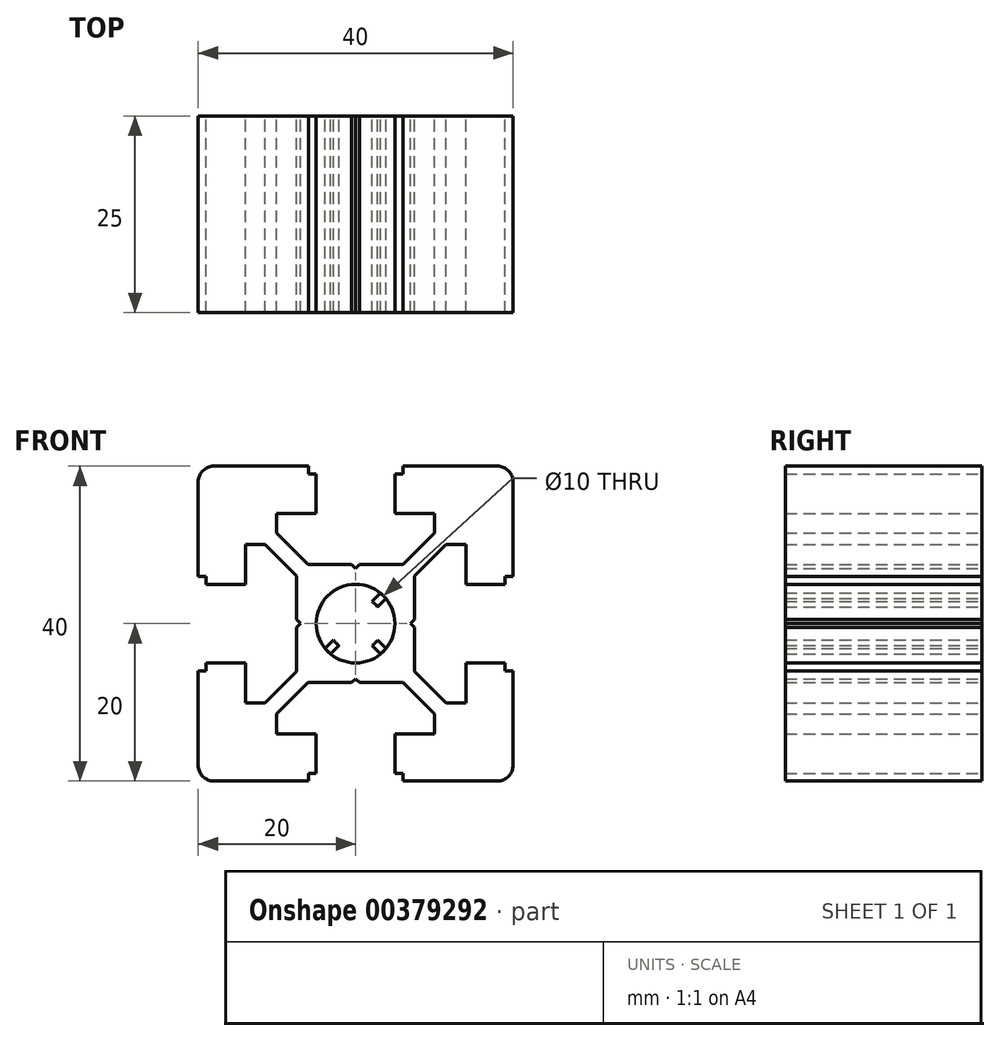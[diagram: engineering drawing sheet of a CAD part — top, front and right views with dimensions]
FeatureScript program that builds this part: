
annotation { "Feature Type Name" : "Feature", "Feature Type Description" : "" }
export const myFeature = defineFeature(function(context is Context, id is Id, definition is map)
    precondition{}
    {
        {
            var Q0;
            Q0=qCreatedBy(makeId("Front.planeOp"),FACE);
            var sketch = newSketch(context, id + "F0", { "sketchPlane" : qUnion([Q0])});
            skLineSegment(sketch, "E0.bottom", {"start": v(2, 0) * mm, "end": v(38, 0) * mm});
            skLineSegment(sketch, "E0.top", {"start": v(2, 40) * mm, "end": v(38, 40) * mm});
            skLineSegment(sketch, "E0.left", {"start": v(0, 2) * mm, "end": v(0, 38) * mm});
            skLineSegment(sketch, "E0.right", {"start": v(40, 2) * mm, "end": v(40, 38) * mm});
            skPoint(sketch, "E1.visualSharp", {"position": v(40, 40) * mm});
            skArc(sketch, "E1.filletArc", {"start": v(40, 38) * mm, "mid": v(39.41, 39.41) * mm, "end": v(38, 40) * mm});
            skPoint(sketch, "E2.visualSharp", {"position": v(0, 40) * mm});
            skArc(sketch, "E2.filletArc", {"start": v(2, 40) * mm, "mid": v(0.59, 39.41) * mm, "end": v(0, 38) * mm});
            skPoint(sketch, "E3.visualSharp", {"position": v(0, 0) * mm});
            skArc(sketch, "E3.filletArc", {"start": v(0, 2) * mm, "mid": v(0.59, 0.59) * mm, "end": v(2, 0) * mm});
            skPoint(sketch, "E4.visualSharp", {"position": v(40, 0) * mm});
            skArc(sketch, "E4.filletArc", {"start": v(38, 0) * mm, "mid": v(39.41, 0.59) * mm, "end": v(40, 2) * mm});
            skLineSegment(sketch, "E5", {"start": v(0, 0) * mm, "end": v(40, 40) * mm, "construction": true});
            skLineSegment(sketch, "E6", {"start": v(0, 40) * mm, "end": v(40, 0) * mm, "construction": true});
            skCircle(sketch, "E7", {"center": v(20, 20) * mm, "radius": 5 * mm});
            skCircle(sketch, "E8", {"center": v(20, 20) * mm, "radius": 3.5 * mm});
            skLineSegment(sketch, "E9.bottom", {"start": v(16.13, 16.84) * mm, "end": v(16.84, 16.13) * mm});
            skLineSegment(sketch, "E9.top", {"start": v(23.16, 23.87) * mm, "end": v(23.87, 23.16) * mm});
            skLineSegment(sketch, "E9.left", {"start": v(16.13, 16.84) * mm, "end": v(23.16, 23.87) * mm});
            skLineSegment(sketch, "E9.right", {"start": v(16.84, 16.13) * mm, "end": v(23.87, 23.16) * mm});
            skLineSegment(sketch, "E10.bottom", {"start": v(16.13, 23.16) * mm, "end": v(16.84, 23.87) * mm});
            skLineSegment(sketch, "E10.top", {"start": v(23.16, 16.13) * mm, "end": v(23.87, 16.84) * mm});
            skLineSegment(sketch, "E10.left", {"start": v(16.13, 23.16) * mm, "end": v(23.16, 16.13) * mm});
            skLineSegment(sketch, "E10.right", {"start": v(16.84, 23.87) * mm, "end": v(23.87, 16.84) * mm});
            skLineSegment(sketch, "E11", {"start": v(14, 40) * mm, "end": v(14, 39) * mm});
            skLineSegment(sketch, "E12", {"start": v(14, 39) * mm, "end": v(15, 39) * mm});
            skLineSegment(sketch, "E13", {"start": v(15, 39) * mm, "end": v(15, 34) * mm});
            skLineSegment(sketch, "E14", {"start": v(15, 34) * mm, "end": v(9.95, 34) * mm});
            skLineSegment(sketch, "E15", {"start": v(9.95, 34) * mm, "end": v(9.95, 31.5) * mm});
            skLineSegment(sketch, "E16", {"start": v(13.95, 27.5) * mm, "end": v(9.95, 31.5) * mm});
            skLineSegment(sketch, "E17", {"start": v(13.95, 27.5) * mm, "end": v(26.05, 27.5) * mm});
            skLineSegment(sketch, "E18", {"start": v(26.05, 27.5) * mm, "end": v(30.05, 31.5) * mm});
            skLineSegment(sketch, "E19", {"start": v(30.05, 31.5) * mm, "end": v(30.05, 34) * mm});
            skLineSegment(sketch, "E20", {"start": v(30.05, 34) * mm, "end": v(25, 34) * mm});
            skLineSegment(sketch, "E21", {"start": v(25, 34) * mm, "end": v(25, 39) * mm});
            skLineSegment(sketch, "E22", {"start": v(25, 39) * mm, "end": v(26, 39) * mm});
            skLineSegment(sketch, "E23", {"start": v(26, 39) * mm, "end": v(26, 40) * mm});
            skLineSegment(sketch, "E24", {"start": v(20, 40) * mm, "end": v(20, -1.4) * mm, "construction": true});
            skLineSegment(sketch, "E25.1.0", {"start": v(6, 9.95) * mm, "end": v(8.5, 9.95) * mm});
            skLineSegment(sketch, "E25.1.1", {"start": v(6, 15) * mm, "end": v(6, 9.95) * mm});
            skLineSegment(sketch, "E25.1.2", {"start": v(1, 15) * mm, "end": v(6, 15) * mm});
            skLineSegment(sketch, "E25.1.3", {"start": v(1, 14) * mm, "end": v(1, 15) * mm});
            skLineSegment(sketch, "E25.1.4", {"start": v(0, 14) * mm, "end": v(1, 14) * mm});
            skLineSegment(sketch, "E25.1.5", {"start": v(12.5, 13.95) * mm, "end": v(8.5, 9.95) * mm});
            skLineSegment(sketch, "E25.1.6", {"start": v(12.5, 13.95) * mm, "end": v(12.5, 26.05) * mm});
            skLineSegment(sketch, "E25.1.7", {"start": v(12.5, 26.05) * mm, "end": v(8.5, 30.05) * mm});
            skLineSegment(sketch, "E25.1.8", {"start": v(8.5, 30.05) * mm, "end": v(6, 30.05) * mm});
            skLineSegment(sketch, "E25.1.9", {"start": v(6, 30.05) * mm, "end": v(6, 25) * mm});
            skLineSegment(sketch, "E25.1.10", {"start": v(6, 25) * mm, "end": v(1, 25) * mm});
            skLineSegment(sketch, "E25.1.11", {"start": v(1, 25) * mm, "end": v(1, 26) * mm});
            skLineSegment(sketch, "E25.1.12", {"start": v(1, 26) * mm, "end": v(0, 26) * mm});
            skLineSegment(sketch, "E25.2.0", {"start": v(30.05, 6) * mm, "end": v(30.05, 8.5) * mm});
            skLineSegment(sketch, "E25.2.1", {"start": v(25, 6) * mm, "end": v(30.05, 6) * mm});
            skLineSegment(sketch, "E25.2.2", {"start": v(25, 1) * mm, "end": v(25, 6) * mm});
            skLineSegment(sketch, "E25.2.3", {"start": v(26, 1) * mm, "end": v(25, 1) * mm});
            skLineSegment(sketch, "E25.2.4", {"start": v(26, 0) * mm, "end": v(26, 1) * mm});
            skLineSegment(sketch, "E25.2.5", {"start": v(26.05, 12.5) * mm, "end": v(30.05, 8.5) * mm});
            skLineSegment(sketch, "E25.2.6", {"start": v(26.05, 12.5) * mm, "end": v(13.95, 12.5) * mm});
            skLineSegment(sketch, "E25.2.7", {"start": v(13.95, 12.5) * mm, "end": v(9.95, 8.5) * mm});
            skLineSegment(sketch, "E25.2.8", {"start": v(9.95, 8.5) * mm, "end": v(9.95, 6) * mm});
            skLineSegment(sketch, "E25.2.9", {"start": v(9.95, 6) * mm, "end": v(15, 6) * mm});
            skLineSegment(sketch, "E25.2.10", {"start": v(15, 6) * mm, "end": v(15, 1) * mm});
            skLineSegment(sketch, "E25.2.11", {"start": v(15, 1) * mm, "end": v(14, 1) * mm});
            skLineSegment(sketch, "E25.2.12", {"start": v(14, 1) * mm, "end": v(14, 0) * mm});
            skLineSegment(sketch, "E25.3.0", {"start": v(34, 30.05) * mm, "end": v(31.5, 30.05) * mm});
            skLineSegment(sketch, "E25.3.1", {"start": v(34, 25) * mm, "end": v(34, 30.05) * mm});
            skLineSegment(sketch, "E25.3.2", {"start": v(39, 25) * mm, "end": v(34, 25) * mm});
            skLineSegment(sketch, "E25.3.3", {"start": v(39, 26) * mm, "end": v(39, 25) * mm});
            skLineSegment(sketch, "E25.3.4", {"start": v(40, 26) * mm, "end": v(39, 26) * mm});
            skLineSegment(sketch, "E25.3.5", {"start": v(27.5, 26.05) * mm, "end": v(31.5, 30.05) * mm});
            skLineSegment(sketch, "E25.3.6", {"start": v(27.5, 26.05) * mm, "end": v(27.5, 13.95) * mm});
            skLineSegment(sketch, "E25.3.7", {"start": v(27.5, 13.95) * mm, "end": v(31.5, 9.95) * mm});
            skLineSegment(sketch, "E25.3.8", {"start": v(31.5, 9.95) * mm, "end": v(34, 9.95) * mm});
            skLineSegment(sketch, "E25.3.9", {"start": v(34, 9.95) * mm, "end": v(34, 15) * mm});
            skLineSegment(sketch, "E25.3.10", {"start": v(34, 15) * mm, "end": v(39, 15) * mm});
            skLineSegment(sketch, "E25.3.11", {"start": v(39, 15) * mm, "end": v(39, 14) * mm});
            skLineSegment(sketch, "E25.3.12", {"start": v(39, 14) * mm, "end": v(40, 14) * mm});
            skLineSegment(sketch, "E26", {"start": v(19.5, 27.5) * mm, "end": v(20, 27) * mm});
            skLineSegment(sketch, "E27", {"start": v(20, 27) * mm, "end": v(20.5, 27.5) * mm});
            skLineSegment(sketch, "E28.1.0", {"start": v(13, 20) * mm, "end": v(12.5, 20.5) * mm});
            skLineSegment(sketch, "E28.1.1", {"start": v(12.5, 19.5) * mm, "end": v(13, 20) * mm});
            skLineSegment(sketch, "E28.2.0", {"start": v(20, 13) * mm, "end": v(19.5, 12.5) * mm});
            skLineSegment(sketch, "E28.2.1", {"start": v(20.5, 12.5) * mm, "end": v(20, 13) * mm});
            skLineSegment(sketch, "E28.3.0", {"start": v(27, 20) * mm, "end": v(27.5, 19.5) * mm});
            skLineSegment(sketch, "E28.3.1", {"start": v(27.5, 20.5) * mm, "end": v(27, 20) * mm});
            skSolve(sketch);
        }
        {
            var Q0;
            {var subQ2=sQuery(id+"F0.wireOp",EDGE,"E1.filletArc");Q0=makeQuery(id+"F0.imprint","IMPRINT",FACE,{"disambiguationData":[TD([[makeQuery(id+"F0.imprint","IMPRINT",EDGE,{"derivedFrom":subQ2}),1.0]])]});}
            var Q1;
            {var subQ3=sQuery(id+"F0.wireOp",EDGE,"E10.left");var subQ5=sQuery(id+"F0.wireOp",EDGE,"E8");var subQ7=makeQuery(id+"F0.imprint","INTERSECT",VERTEX,{"disambiguationData":[OD(0.0)],"derivedFrom":[subQ5,subQ3]});Q1=makeQuery(id+"F0.imprint","IMPRINT",FACE,{"disambiguationData":[TD([[makeQuery(id+"F0.imprint","IMPRINT",EDGE,{"disambiguationData":[TD([[subQ7,-1.0]])],"derivedFrom":subQ5}),-1.0]])]});}
            var Q2;
            {var subQ0=sQuery(id+"F0.wireOp",EDGE,"E9.right");var subQ5=sQuery(id+"F0.wireOp",EDGE,"E8");var subQ6=makeQuery(id+"F0.imprint","INTERSECT",VERTEX,{"disambiguationData":[OD(1.0)],"derivedFrom":[subQ5,subQ0]});Q2=makeQuery(id+"F0.imprint","IMPRINT",FACE,{"disambiguationData":[TD([[makeQuery(id+"F0.imprint","IMPRINT",EDGE,{"disambiguationData":[TD([[subQ6,-1.0]])],"derivedFrom":subQ5}),-1.0]])]});}
            var Q3;
            {var subQ0=sQuery(id+"F0.wireOp",EDGE,"E9.right");var subQ5=sQuery(id+"F0.wireOp",EDGE,"E8");var subQ6=makeQuery(id+"F0.imprint","INTERSECT",VERTEX,{"disambiguationData":[OD(0.0)],"derivedFrom":[subQ5,subQ0]});Q3=makeQuery(id+"F0.imprint","IMPRINT",FACE,{"disambiguationData":[TD([[makeQuery(id+"F0.imprint","IMPRINT",EDGE,{"disambiguationData":[TD([[subQ6,1.0]])],"derivedFrom":subQ5}),-1.0]])]});}
            var Q4;
            {var subQ0=sQuery(id+"F0.wireOp",EDGE,"E9.left");var subQ5=sQuery(id+"F0.wireOp",EDGE,"E8");var subQ6=makeQuery(id+"F0.imprint","INTERSECT",VERTEX,{"disambiguationData":[OD(0.0)],"derivedFrom":[subQ5,subQ0]});Q4=makeQuery(id+"F0.imprint","IMPRINT",FACE,{"disambiguationData":[TD([[makeQuery(id+"F0.imprint","IMPRINT",EDGE,{"disambiguationData":[TD([[subQ6,-1.0]])],"derivedFrom":subQ5}),-1.0]])]});}
            extrude(context, id + "F1", {"entities" : qUnion([Q0, Q1, Q2, Q3, Q4]), "offsetDistance" : 25 * mm, "depth" : 25 * mm});
        }
    });
